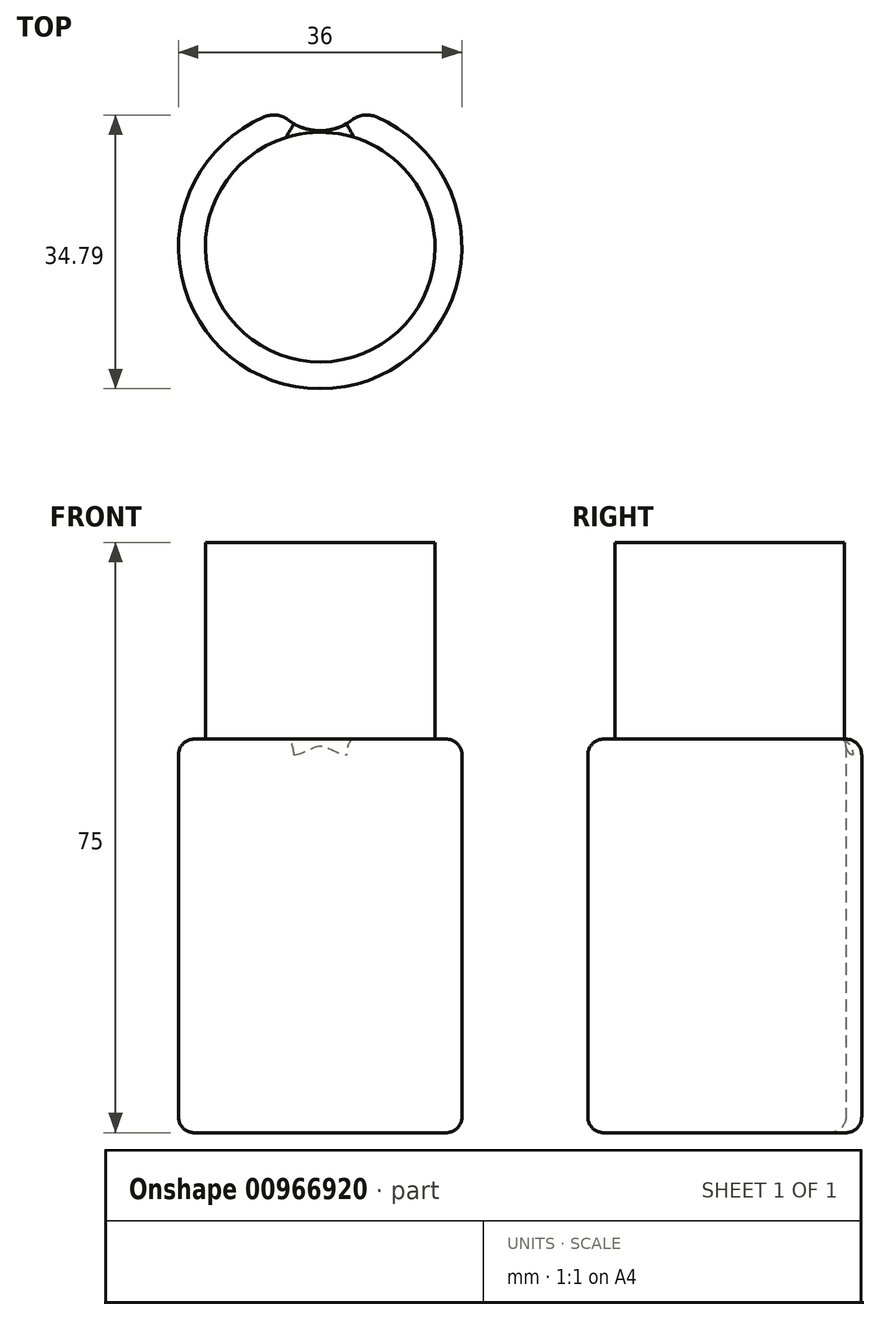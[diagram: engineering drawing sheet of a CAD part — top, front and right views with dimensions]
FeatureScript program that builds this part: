
annotation { "Feature Type Name" : "Feature", "Feature Type Description" : "" }
export const myFeature = defineFeature(function(context is Context, id is Id, definition is map)
    precondition{}
    {
        {
            var Q0;
            Q0=qCreatedBy(makeId("Top.planeOp"),FACE);
            var sketch = newSketch(context, id + "F0", { "sketchPlane" : qUnion([Q0])});
            skCircle(sketch, "E0", {"center": v(0, 0) * mm, "radius": 18 * mm});
            skSolve(sketch);
        }
        {
            var Q0;
            Q0=makeQuery(id+"F0.imprint","IMPRINT",FACE,{"disambiguationData":[TD([[makeQuery(id+"F0.imprint","IMPRINT",EDGE,{"derivedFrom":sQuery(id+"F0.wireOp",EDGE,"E0")}),1.0]])]});
            extrude(context, id + "F1", {"entities" : qUnion([Q0]), "depth" : 50 * mm, "offsetDistance" : 25 * mm});
        }
        {
            var Q0;
            Q0=qCreatedBy(makeId("Top.planeOp"),FACE);
            var sketch = newSketch(context, id + "F2", { "sketchPlane" : qUnion([Q0])});
            skCircle(sketch, "E1", {"center": v(0, 21.51) * mm, "radius": 6.73 * mm});
            skSolve(sketch);
        }
        {
            var Q0;
            Q0=qCreatedBy(makeId("Front.planeOp"),FACE);
            var sketch = newSketch(context, id + "F3", { "sketchPlane" : qUnion([Q0])});
            skLineSegment(sketch, "E2", {"start": v(0, -16.04) * mm, "end": v(0, 37.16) * mm});
            skSolve(sketch);
        }
        {
            var Q0;
            Q0=makeQuery(id+"F2.imprint","IMPRINT",FACE,{"disambiguationData":[TD([[makeQuery(id+"F2.imprint","IMPRINT",EDGE,{"derivedFrom":sQuery(id+"F2.wireOp",EDGE,"E1")}),1.0]])]});
            extrude(context, id + "F4", {"entities" : qUnion([Q0]), "operationType" : NewBodyOperationType.REMOVE, "depth" : 50 * mm, "offsetDistance" : 25 * mm});
        }
        {
            var Q0;
            Q0=makeQuery(id+"F4.boolean.opBoolean","INTERSECT",EDGE,{"disambiguationData":[OD(1.0)],"derivedFrom":[makeQuery(id+"F1.opExtrude","SWEPT_FACE",FACE,{"disambiguationData":[OSD([sQuery(id+"F0.wireOp",EDGE,"E0")])]}),makeQuery(id+"F4.opExtrude","SWEPT_FACE",FACE,{"disambiguationData":[OSD([sQuery(id+"F2.wireOp",EDGE,"E1")])]})]});
            var Q1;
            Q1=makeQuery(id+"F4.boolean.opBoolean","INTERSECT",EDGE,{"disambiguationData":[OD(0.0)],"derivedFrom":[makeQuery(id+"F1.opExtrude","SWEPT_FACE",FACE,{"disambiguationData":[OSD([sQuery(id+"F0.wireOp",EDGE,"E0")])]}),makeQuery(id+"F4.opExtrude","SWEPT_FACE",FACE,{"disambiguationData":[OSD([sQuery(id+"F2.wireOp",EDGE,"E1")])]})]});
            fillet(context, id + "F5", {"entities" : qUnion([Q0, Q1]), "radius" : 3 * mm, "tangentPropagation" : true, "allowEdgeOverflow" : false});
        }
        {
            var Q0;
            Q0=makeQuery(id+"F1.opExtrude","CAP_FACE",FACE,{"disambiguationData":[OSD([sQuery(id+"F0.wireOp",EDGE,"E0")])],"isStart":true});
            fillet(context, id + "F6", {"entities" : qUnion([Q0]), "radius" : 2 * mm, "tangentPropagation" : true, "allowEdgeOverflow" : false});
        }
        {
            var Q0;
            Q0=makeQuery(id+"F1.opExtrude","CAP_FACE",FACE,{"disambiguationData":[OSD([sQuery(id+"F0.wireOp",EDGE,"E0")])],"isStart":false});
            cPlane(context, id + "F7", {"entities" : qUnion([Q0]), "cplaneType" : CPlaneType.OFFSET, "offset" : 0 * mm, "width" : 150 * mm, "height" : 150 * mm});
        }
        {
            var Q0;
            Q0=qCreatedBy(id+"F7.planeOp",FACE);
            var sketch = newSketch(context, id + "F8", { "sketchPlane" : qUnion([Q0])});
            skCircle(sketch, "E3", {"center": v(0, 0) * mm, "radius": 14.59 * mm});
            skSolve(sketch);
        }
        {
            var Q0;
            Q0=makeQuery(id+"F8.imprint","IMPRINT",FACE,{"disambiguationData":[TD([[makeQuery(id+"F8.imprint","IMPRINT",EDGE,{"derivedFrom":sQuery(id+"F8.wireOp",EDGE,"E3")}),1.0]])]});
            extrude(context, id + "F9", {"entities" : qUnion([Q0]), "operationType" : NewBodyOperationType.ADD, "depth" : 25 * mm, "offsetDistance" : 25 * mm});
        }
        {
            var Q0;
            {var subQ0=sQuery(id+"F0.wireOp",EDGE,"E0");var subQ1=makeQuery(id+"F1.opExtrude","SWEPT_FACE",FACE,{"disambiguationData":[OSD([subQ0])]});var subQ2=sQuery(id+"F2.wireOp",EDGE,"E1");Q0=makeQuery(id+"FAHDAe0IvvkEzgC_1.1.F4.boolean.opBoolean","SPLIT",EDGE,{"disambiguationData":[TD([makeQuery(id+"F5.opFillet","BLEND_FACE",FACE,{"disambiguationData":[OSD([subQ0,subQ2]),TDD([makeQuery(id+"F4.boolean.opBoolean","INTERSECT",EDGE,{"disambiguationData":[OD(0.0)],"derivedFrom":[subQ1,makeQuery(id+"F4.opExtrude","SWEPT_FACE",FACE,{"disambiguationData":[OSD([subQ2])]})]})])]})])],"derivedFrom":makeQuery(id+"F1.opExtrude","CAP_EDGE",EDGE,{"disambiguationData":[OSD([subQ0])],"isStart":false})});}
            fillet(context, id + "F10", {"entities" : qUnion([Q0]), "radius" : 2 * mm, "tangentPropagation" : true, "allowEdgeOverflow" : false});
        }
    });
